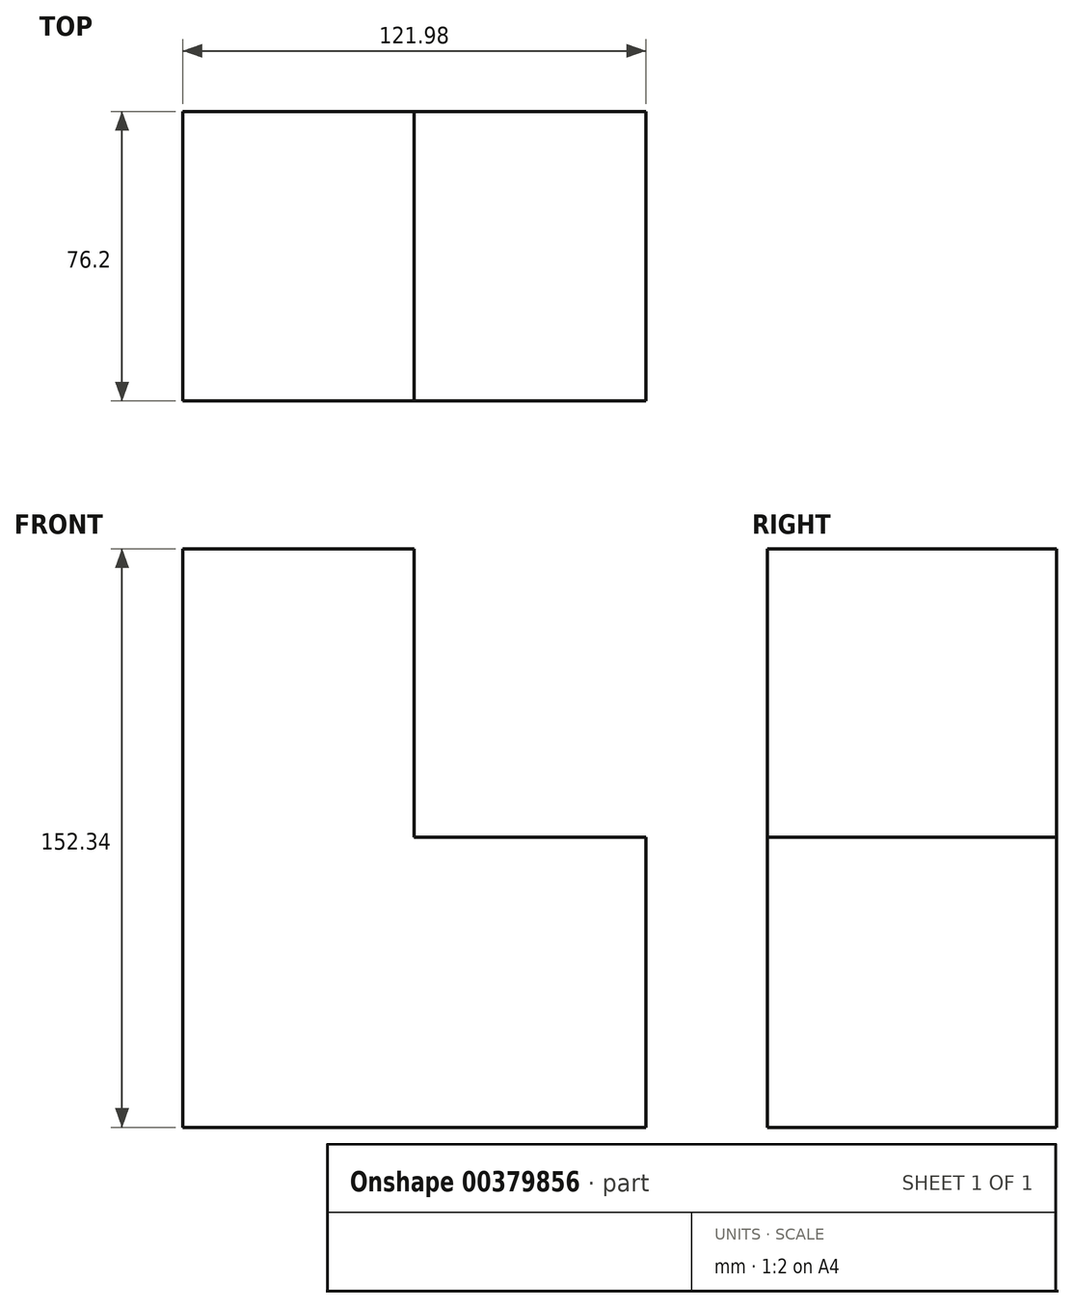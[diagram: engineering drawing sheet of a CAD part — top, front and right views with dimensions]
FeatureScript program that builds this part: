
annotation { "Feature Type Name" : "Feature", "Feature Type Description" : "" }
export const myFeature = defineFeature(function(context is Context, id is Id, definition is map)
    precondition{}
    {
        {
            var Q0;
            Q0=qCreatedBy(makeId("Front.planeOp"),FACE);
            var sketch = newSketch(context, id + "F0", { "sketchPlane" : qUnion([Q0])});
            skLineSegment(sketch, "E0", {"start": v(-76.07, 75.98) * mm, "end": v(-15.18, 75.98) * mm});
            skLineSegment(sketch, "E1", {"start": v(-15.18, 75.98) * mm, "end": v(-15.18, 0) * mm});
            skLineSegment(sketch, "E2", {"start": v(-15.18, 0) * mm, "end": v(45.91, 0) * mm});
            skLineSegment(sketch, "E3", {"start": v(45.91, 0) * mm, "end": v(45.91, -76.36) * mm});
            skLineSegment(sketch, "E4", {"start": v(45.91, -76.36) * mm, "end": v(-76.07, -76.36) * mm});
            skLineSegment(sketch, "E5", {"start": v(-76.07, -76.36) * mm, "end": v(-76.07, 75.98) * mm});
            skSolve(sketch);
        }
        {
            var Q0;
            Q0 = qSketchRegion(id + "F0", true);
            var Q1;
            Q1=makeQuery(id+"F0.imprint","IMPRINT",FACE,{"disambiguationData":[TD([[makeQuery(id+"F0.imprint","IMPRINT",EDGE,{"derivedFrom":sQuery(id+"F0.wireOp",EDGE,"E0")}),-1.0]])]});
            extrude(context, id + "F1", {"entities" : qUnion([Q0, Q1]), "depth" : 76.2 * mm});
        }
    });
